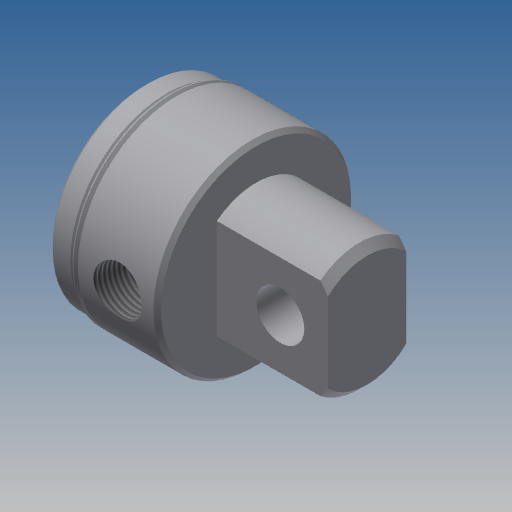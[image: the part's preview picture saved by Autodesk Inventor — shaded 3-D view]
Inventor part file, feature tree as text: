
AUTODESK INVENTOR PART (.ipt)
format: ipt  version: 2020 (Build 240168000, 168)  size: 292,864 bytes
history: native  units: in
note: dims shown in document units (in); Inventor stores cm internally (conversion verified against a paired STEP export)
features: other x126, sketch x8, revolve x5, extrude x2, hole x1, thread x1
ambient origin geometry x8: Origin, YZ Plane, XZ Plane, XY Plane, X Axis, Y Axis, Z Axis, Center Point
bodies: Solid1 (feature_tree)
feature tree (143):
  revolve  "Revolution1"  Angle=360.0deg
  revolve  "Revolution2"  Angle=360.0deg
  extrude  "Extrusion1"  TaperAngle=360.0deg  [1 undecoded]
  hole  "Hole1"  [1 undecoded]
  revolve  "Revolution3"  [1 undecoded]
  thread  "Thread1"  [1 undecoded]
  revolve  "Revolution4"  [1 undecoded]
  revolve  "Revolution5"  [1 undecoded]
  extrude  "Extrusion2"  [1 undecoded]
  other  "f_XY"
  other  "f_YZ"
  other  "f_ZX"
  other  "f_X"
  other  "f_Y"
  other  "f_Z"
  other  "f_Center"
  other  "lovra1_XY"
  other  "lovra1_YZ"
  other  "lovra1_ZX"
  other  "lovra1_X"
  other  "lovra1_Y"
  other  "lovra1_Z"
  other  "lovra1_Center"
  other  "lovra2_XY"
  other  "lovra2_YZ"
  other  "lovra2_ZX"
  other  "lovra2_X"
  other  "lovra2_Y"
  other  "lovra2_Z"
  other  "lovra2_Center"
  other  "lovra21_XY"
  other  "lovra21_YZ"
  other  "lovra21_ZX"
  other  "lovra21_X"
  other  "lovra21_Y"
  other  "lovra21_Z"
  other  "lovra21_Center"
  other  "lovra22_XY"
  other  "lovra22_YZ"
  other  "lovra22_ZX"
  other  "lovra22_X"
  other  "lovra22_Y"
  other  "lovra22_Z"
  other  "lovra22_Center"
  other  "lovra3_XY"
  other  "lovra3_YZ"
  other  "lovra3_ZX"
  other  "lovra3_X"
  other  "lovra3_Y"
  other  "lovra3_Z"
  other  "lovra3_Center"
  other  "olen_XY"
  other  "olen_YZ"
  other  "olen_ZX"
  other  "olen_X"
  other  "olen_Y"
  other  "olen_Z"
  other  "olen_Center"
  other  "p1_XY"
  other  "p1_YZ"
  other  "p1_ZX"
  other  "p1_X"
  other  "p1_Y"
  other  "p1_Z"
  other  "p1_Center"
  other  "p2_XY"
  other  "p2_YZ"
  other  "p2_ZX"
  other  "p2_X"
  other  "p2_Y"
  other  "p2_Z"
  other  "p2_Center"
  other  "port_XY"
  other  "port_YZ"
  other  "port_ZX"
  other  "port_X"
  other  "port_Y"
  other  "port_Z"
  other  "port_Center"
  other  "port2_XY"
  other  "port2_YZ"
  other  "port2_ZX"
  other  "port2_X"
  other  "port2_Y"
  other  "port2_Z"
  other  "port2_Center"
  other  "thd1_XY"
  other  "thd1_YZ"
  other  "thd1_ZX"
  other  "thd1_X"
  other  "thd1_Y"
  other  "thd1_Z"
  other  "thd1_Center"
  other  "thd2_XY"
  other  "thd2_YZ"
  other  "thd2_ZX"
  other  "thd2_X"
  other  "thd2_Y"
  other  "thd2_Z"
  other  "thd2_Center"
  other  "to_mounting_bracket_XY"
  other  "to_mounting_bracket_YZ"
  other  "to_mounting_bracket_ZX"
  other  "to_mounting_bracket_X"
  other  "to_mounting_bracket_Y"
  other  "to_mounting_bracket_Z"
  other  "to_mounting_bracket_Center"
  other  "to_nut_XY"
  other  "to_nut_YZ"
  other  "to_nut_ZX"
  other  "to_nut_X"
  other  "to_nut_Y"
  other  "to_nut_Z"
  other  "to_nut_Center"
  other  "to_pin_XY"
  other  "to_pin_YZ"
  other  "to_pin_ZX"
  other  "to_pin_X"
  other  "to_pin_Y"
  other  "to_pin_Z"
  other  "to_pin_Center"
  other  "to_screw_XY"
  other  "to_screw_YZ"
  other  "to_screw_ZX"
  other  "to_screw_X"
  other  "to_screw_Y"
  other  "to_screw_Z"
  other  "to_screw_Center"
  other  "to_tube_XY"
  other  "to_tube_YZ"
  other  "to_tube_ZX"
  other  "to_tube_X"
  other  "to_tube_Y"
  other  "to_tube_Z"
  other  "to_tube_Center"
  sketch  "Sketch_18"  dims[d4=0.532in d5=0.75in d6=0.375in d7=0.25in d8=0.5635in d9=0.8052in d10=120.0deg d11=360.0deg]
  sketch  "Sketch_21"  dims[d15=360.0deg d16=0.9255in d17=0.0in]
  sketch  "Sketch_9"  dims[d2=0.875in d3=0.0in]
  sketch  "Sketch4"  dims[d0=360.0deg d1=360.0deg]
  sketch  "Sketch_68"
  sketch  "Sketch_20"  dims[d12=0.2731in d13=0.0in d14=360.0deg]
  sketch  "Sketch_24"  dims[d18=0.0in d19=0.0in d20=0.0in d21=0.0in d22=0.0in d23=0.0in d24=0.0in d25=0.0in d26=0.0in]
  sketch  "Sketch_43"
note: 7 required parameter values undecoded (feature->parameter linkage not recoverable at this tier; creation-order binding heuristic only, values carry confidence <= 0.55)
